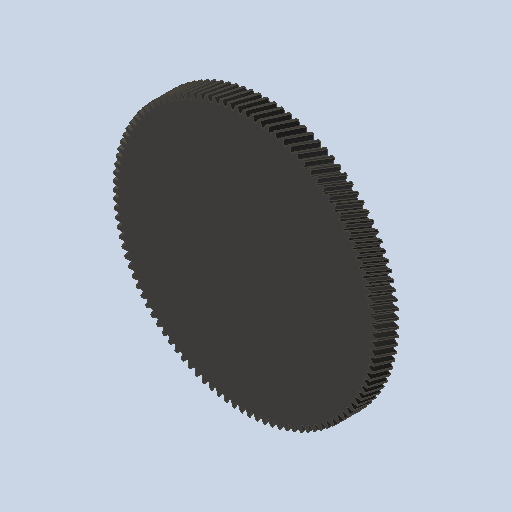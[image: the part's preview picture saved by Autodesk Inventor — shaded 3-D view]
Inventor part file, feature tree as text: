
AUTODESK INVENTOR PART (.ipt)
format: ipt  version: 2023 (Build 270158000, 158)  size: 1,263,104 bytes
history: native  units: mm (DEFAULTED — no unit token found)
features: plane x3, other x3, sketch x2, extrude x1
ambient origin geometry x8: Origin, YZ Plane, XZ Plane, XY Plane, X Axis, Y Axis, Z Axis, Center Point
bodies: Solid1 (feature_tree)
feature tree (9):
  extrude  "Extrusion1"  Depth=15.0mm TaperAngle=0.0deg
  plane  "Work Plane2"
  plane  "Work Plane8"
  plane  "Work Plane9"
  other  "Spur Gear"
  sketch  "Sketch1"  dims[d0=174.274667mm d1=15.0mm d2=0.0mm]
  sketch  "Sketch2"  dims[d3=170.800532mm d4=10.0mm d5=0.0mm d16=2.25mm d17=0.0mm d34=0.293607mm d39=0.0mm d41=0.0mm d43=2.25mm d46=2.25mm d47=0.0mm d48=0.0mm]
  other  "Srf1"
  other  "Pitch Diameter"
